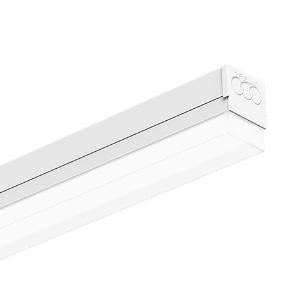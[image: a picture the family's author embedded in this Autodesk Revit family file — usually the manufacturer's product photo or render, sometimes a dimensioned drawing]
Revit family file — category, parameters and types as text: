
# Revit family: 3f_filippi_-_3f_linux_dr_3f_filippi_-_a20525_-_3f_linux_dr_2x30_led_dali_l1778
name_source: partatom
category: Lighting Fixtures
units: mm (PartAtom-declared; Revit-internal decimal feet)

## family parameters
Cut with Voids When Loaded = No
Host = Face
Light Source = No
Part Type = Normal
Room Calculation Point = No
Round Connector Dimension = Use Diameter
Shared = No

## types (1)
- 3F Filippi - 3F Linux DR (1 x LED, 7856 lm, 66 W, 4000 K)
    Apparent Load = 66 VA
    Approval mark = CE
    CIE Flux Codes = 41 72 91 86 100
    Color Rendering = 80
    Color Temperature = 4000 K
    Control Gear = Electronic transformer
    Default Elevation = 1800 mm
    Description = Light unit for structure continues 3F Linux S.

ILLUMINOTECHNICAL
Luminous efficiency 100% (DLOR 86%, ULOR 14%).
Initial luminous flux of the luminaire 7856 lm.
Diffused symmetric distribution.
Installation Interdistance Transv.D = 1.38 x hu - Long.D = 1.25 x hu.
Tabular UGR (CIE 117 - 4H-8H; S=0.25H; 70/50/20): RUG 25.8 - 24.4.
Beam angle: 136° - 112°.
Luminous efficacy 119 lm/W.
Lifetime (L93/B10): 30000 h. (tq+25°C)
Lifetime (L90/B10): 50000 h. (tq+25°C)
Lifetime (L85/B10): 80000 h. (tq+25°C)
Lifetime (L80/B10): 100000 h. (tq+25°C)
Sudden decreased luminous flux after 50000 hours: 0% (C0).
Photobiological safety in compliance with IEC/TR 62778: RG0 risk exempt, (IEC 62471).
In compliance with IEC/EN 62722-2-1 - IEC/EN 62717 standards.

SOURCE
2 linear LED modules 30W/840.
Energy efficiency class (UE 2019/2020 - UE 2019/2015): D.
CIE 13.3 Colour rendering index: CRI >80 (R9 <50%).
IES TM-30 Fidelity Index: Rf = 84 Rg = 95.
CCT nominal colour temperature 4000 K.
Colour initial tolerance (MacAdam): SDCM 3.

MECHANICAL
Light unit in hot-galvanised steel, painted in white polyester base with fixing springs and retractable safety hooks in stainless steel.
Rectangular screen in self-extinguishing polycarbonate, UV stabilised, opal, with smooth outer surface.
Luminaire with limited surface temperature. - D - (EN 60598-2-24)
Dimensions: 1778x62 mm, height 81 mm. Weight 2.485 kg.
IP40 protection degree.
Mechanical strength to impacts IK06 (1 joule).
Glow-wire test resistance 850°C.

ELECTRICAL
Halogen Free DALI-2, PUSH-DIM, electronic wiring 230V-50/60Hz, power factor 0.95 at full load, THD <25%, constant output current, SELV, class I, 1 driver, 1 DALI addresse.
Power of the luminaire 66 W.
ENEC - CE.
SAFE FLICKER: PstLM=<1 and SVM=<0.4 (IEC TR 61547-1 and IEC TR 63158), to ensure a more comfortable and safe light.
Luminaire compliant with EN 60598-2-22 for power supply from a centralised emergency system CPSS (Central Power Supply System), not incorporated in the luminaire - high risk areas excluded. The default power and flux are 100% in AC and 15% in DC.
Ambient temperature from 0°C to +30°C.
Temperature class T6 max 85°C.
Connection to the structure with 5-pin plug with phase selection (H05Z-U Halogen Free cable section 0.5 mm² HT90).
Relative humidity UR: <85%.

INSTALLATION
Ceiling / Suspended / Wall.
All accessories dedicated to this product are available on the Catalog and on our website www.3F-Filippi.com.

STRUCTURE
Hot-galvanised wired structure, painted in polyester base white, obtained through rolling process.
Saline-mist resistance equal to 300hrs and damp resistance equal to 700hrs.
Through-wiring 5 or 7 poles with cables H07Z-U Halogen Free section 2.5 mm² HT90, with quick connecting terminal, irreversible, start / end and intermediate power towers.
Linear connecting element in hot galvanised steel already mounted on one end to form continuous channels, only L3556 structures.
A20017 - 3F Linux S 5P L3556, structure with through-wiring 5-pole.
A20019 - 3F Linux S 5P L1778, structure with through-wiring 5-pole.
A20024 - 3F Linux S 7P L3556, structure with through-wiring 7-pole.
A20026 - 3F Linux S 7P L1778, structure with through-wiring 7-pole.

APPLICATIONS
Suitable product for food production plants (HACCP), IFS (Food Version 6), BRC (GSFS Food Version 7).
In commercial environments, exhibition areas, shops and stores.

LIGHT MANAGEMENT
Recommended minimum setting: 10%.
The device, equipped with DALI-2 driver, can be controlled manually with 3F Easy Dim technology or automatically/manually with 3F Smart Dimming technology and/or centralised DALI systems.
DALI-2 certification guarantees interoperability with other devices with the same certification.
In electrical systems without a regulation system (manual or automatic) and DALI bus, a suitable jumper must be made on the DA-DA terminals of the appliance.

WARNING
Luminaire designed for disposal/recycling at end-of-life.
Replaceable (LED only) light source by a professional. Replaceable control gear by a professional.
    Height = 81 mm
    Lamp = 1 x LED
    Lamp Light Flux = 7856 lm
    Lamp Power = 66 W
    Lamp count = 1
    Length = 1778 mm
    Lifetime = 50000 h
    Luminous efficacy = 119 lm/W
    Manufacturer = 3F Filippi
    ModVariant = No
    Model = 3F Filippi - A20525 - 3F Linux DR 2x30 LED DALI L1778
    Mounting Place = Ceiling
    Mounting Type = Pendant
    Number of Poles = 1
    OnlyDefault = Yes
    Power Factor = 1
    Product Name = 3F Filippi - 3F Linux DR
    Product group = pendant luminaire
    ProductGroupID = 9
    Protection Class = Protection class I
    Protection Degree = IP 40
    RLX_Detail_Level = 1
    RLX_Emergency_Light_Flux = 0 lm
    RLX_Emergency_Type = 0
    RLX_Emergency_Type_DB = No
    RlxData = <blob elided: 35741 chars, md5=7eee568b>
    Socket = socket
    Standby Power = 0 W
    System Light Flux = 7856 lm
    System Power = 66 W
    Type Comments = Product without accessories
    Type Image = 3ffilippi_3f_linux_dr.jpg
    URL = http://relux.com
    VarID = ---
    Voltage = 0 V
    Weight = 0.00 kg
    Width = 62 mm  [stored 0.203412 ft]

note: [stored X ft] marks values corroborated as IEEE doubles in the binary element streams (Revit-internal decimal feet)

## geometry (parser evidence)
native form markers: Blend x4, Sweep x15
no freeform markers — native parametric forms only
